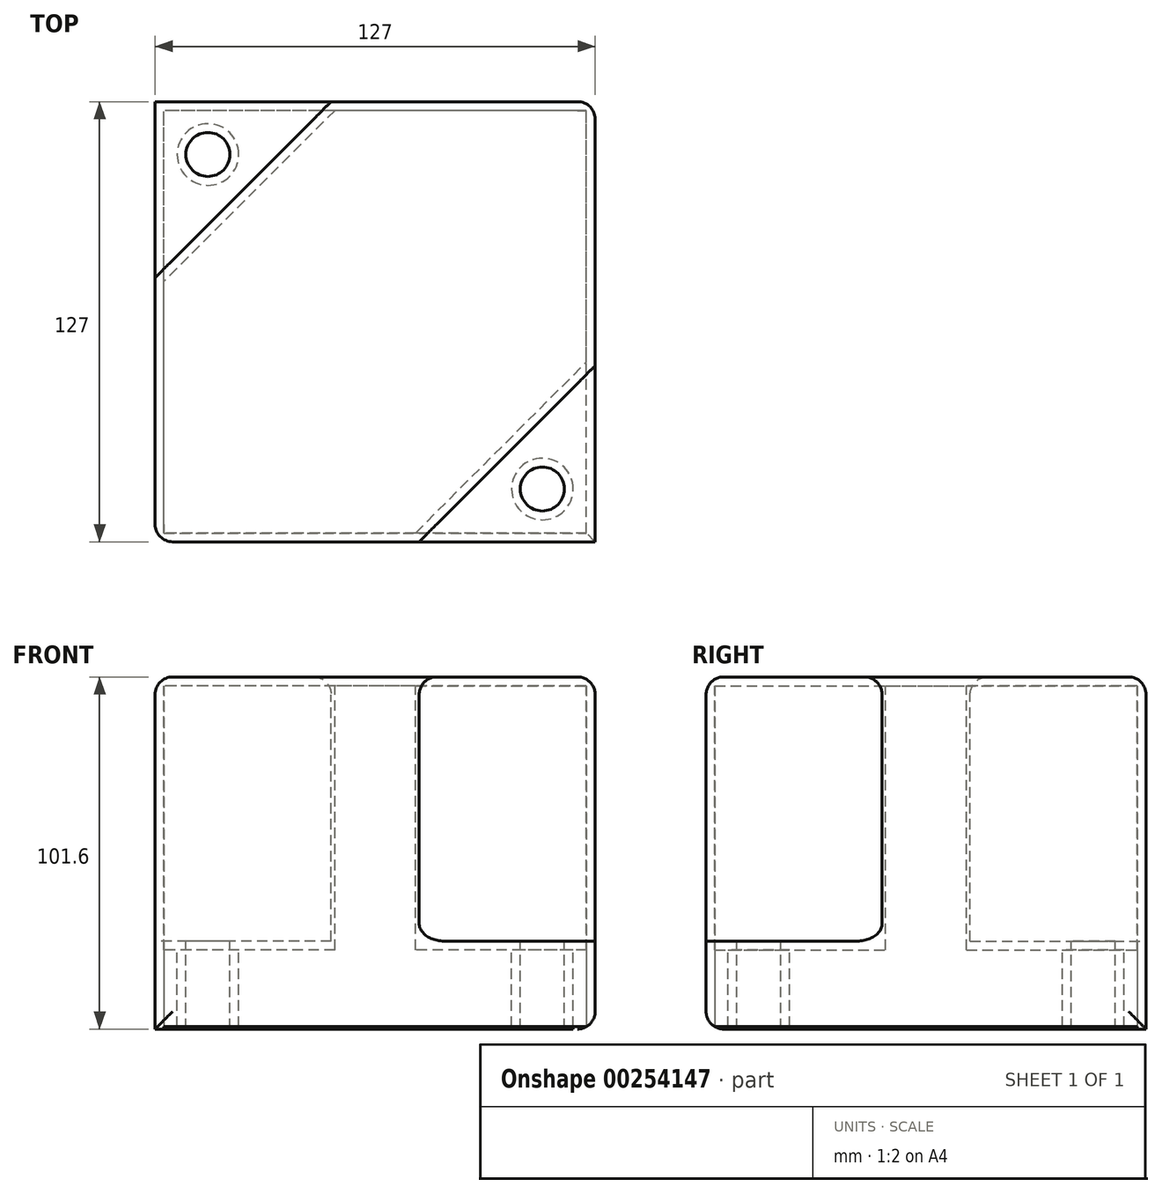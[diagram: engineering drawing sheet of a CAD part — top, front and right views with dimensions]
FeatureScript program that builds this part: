
annotation { "Feature Type Name" : "Feature", "Feature Type Description" : "" }
export const myFeature = defineFeature(function(context is Context, id is Id, definition is map)
    precondition{}
    {
        {
            var Q0;
            Q0=qCreatedBy(makeId("Top.planeOp"),FACE);
            var sketch = newSketch(context, id + "F0", { "sketchPlane" : qUnion([Q0])});
            skLineSegment(sketch, "E0.bottom", {"start": v(63.5, -63.5) * mm, "end": v(-63.5, -63.5) * mm});
            skLineSegment(sketch, "E0.top", {"start": v(63.5, 63.5) * mm, "end": v(-63.5, 63.5) * mm});
            skLineSegment(sketch, "E0.left", {"start": v(63.5, -63.5) * mm, "end": v(63.5, 63.5) * mm});
            skLineSegment(sketch, "E0.right", {"start": v(-63.5, -63.5) * mm, "end": v(-63.5, 63.5) * mm});
            skPoint(sketch, "E0.middle", {"position": v(0, 0) * mm});
            skSolve(sketch);
        }
        {
            var Q0;
            Q0=makeQuery(id+"F0.imprint","IMPRINT",FACE,{"disambiguationData":[TD([[makeQuery(id+"F0.imprint","IMPRINT",EDGE,{"derivedFrom":sQuery(id+"F0.wireOp",EDGE,"E0.bottom")}),-1.0]])]});
            extrude(context, id + "F1", {"entities" : qUnion([Q0]), "depth" : 101.6 * mm});
        }
        {
            var Q0;
            Q0=makeQuery(id+"F1.opExtrude","CAP_FACE",FACE,{"disambiguationData":[OSD([sQuery(id+"F0.wireOp",EDGE,"E0.bottom"),sQuery(id+"F0.wireOp",EDGE,"E0.top"),sQuery(id+"F0.wireOp",EDGE,"E0.left"),sQuery(id+"F0.wireOp",EDGE,"E0.right")])],"isStart":false});
            var sketch = newSketch(context, id + "F2", { "sketchPlane" : qUnion([Q0])});
            skLineSegment(sketch, "E1", {"start": v(-12.7, 63.5) * mm, "end": v(-63.5, 12.7) * mm});
            skLineSegment(sketch, "E2", {"start": v(12.7, -63.5) * mm, "end": v(63.5, -12.7) * mm});
            skSolve(sketch);
        }
        {
            var Q0;
            {var subQ0=sQuery(id+"F2.wireOp",EDGE,"E2");Q0=makeQuery(id+"F2.imprint","IMPRINT",FACE,{"disambiguationData":[TD([[makeQuery(id+"F2.imprint","IMPRINT",EDGE,{"derivedFrom":subQ0}),-1.0]])]});}
            var Q1;
            {var subQ0=sQuery(id+"F2.wireOp",EDGE,"E1");Q1=makeQuery(id+"F2.imprint","IMPRINT",FACE,{"disambiguationData":[TD([[makeQuery(id+"F2.imprint","IMPRINT",EDGE,{"derivedFrom":subQ0}),-1.0]])]});}
            extrude(context, id + "F3", {"entities" : qUnion([Q0, Q1]), "operationType" : NewBodyOperationType.REMOVE, "oppositeDirection" : true, "depth" : 76.2 * mm});
        }
        {
            var Q0;
            Q0=makeQuery(id+"F3.boolean.opBoolean","COPY",FACE,{"derivedFrom":makeQuery(id+"F3.opExtrude","CAP_FACE",FACE,{"disambiguationData":[OSD([sQuery(id+"F0.wireOp",EDGE,"E0.top"),sQuery(id+"F0.wireOp",EDGE,"E0.right"),sQuery(id+"F2.wireOp",EDGE,"E1")])],"isStart":false})});
            var sketch = newSketch(context, id + "F4", { "sketchPlane" : qUnion([Q0])});
            skCircle(sketch, "E3", {"center": v(-48.26, 48.26) * mm, "radius": 6.35 * mm});
            skCircle(sketch, "E4", {"center": v(48.26, -48.26) * mm, "radius": 6.35 * mm});
            skSolve(sketch);
        }
        {
            var Q0;
            Q0=makeQuery(id+"F4.imprint","IMPRINT",FACE,{"disambiguationData":[TD([[makeQuery(id+"F4.imprint","IMPRINT",EDGE,{"derivedFrom":sQuery(id+"F4.wireOp",EDGE,"E3")}),1.0]])]});
            var Q1;
            Q1=makeQuery(id+"F4.imprint","IMPRINT",FACE,{"disambiguationData":[TD([[makeQuery(id+"F4.imprint","IMPRINT",EDGE,{"derivedFrom":sQuery(id+"F4.wireOp",EDGE,"E4")}),1.0]])]});
            extrude(context, id + "F5", {"entities" : qUnion([Q0, Q1]), "operationType" : NewBodyOperationType.REMOVE, "oppositeDirection" : true, "depth" : 203.2 * mm});
        }
        {
            var Q0;
            Q0=makeQuery(id+"F1.opExtrude","CAP_FACE",FACE,{"disambiguationData":[OSD([sQuery(id+"F0.wireOp",EDGE,"E0.bottom"),sQuery(id+"F0.wireOp",EDGE,"E0.top"),sQuery(id+"F0.wireOp",EDGE,"E0.left"),sQuery(id+"F0.wireOp",EDGE,"E0.right")])],"isStart":true});
            shell(context, id + "F6", {"entities" : qUnion([Q0]), "thickness" : 2.54 * mm});
        }
        {
            var Q0;
            Q0=makeQuery(id+"F1.opExtrude","CAP_EDGE",EDGE,{"disambiguationData":[OSD([sQuery(id+"F0.wireOp",EDGE,"E0.right")])],"isStart":false});
            var Q1;
            Q1=makeQuery(id+"F1.opExtrude","CAP_EDGE",EDGE,{"disambiguationData":[OSD([sQuery(id+"F0.wireOp",EDGE,"E0.bottom")])],"isStart":false});
            var Q2;
            Q2=makeQuery(id+"F3.boolean.opBoolean","COPY",EDGE,{"derivedFrom":makeQuery(id+"F3.opExtrude","CAP_EDGE",EDGE,{"disambiguationData":[OSD([sQuery(id+"F2.wireOp",EDGE,"E2")])],"isStart":true})});
            var Q3;
            Q3=makeQuery(id+"F1.opExtrude","CAP_EDGE",EDGE,{"disambiguationData":[OSD([sQuery(id+"F0.wireOp",EDGE,"E0.left")])],"isStart":false});
            var Q4;
            Q4=makeQuery(id+"F1.opExtrude","CAP_EDGE",EDGE,{"disambiguationData":[OSD([sQuery(id+"F0.wireOp",EDGE,"E0.top")])],"isStart":false});
            var Q5;
            Q5=makeQuery(id+"F3.boolean.opBoolean","COPY",EDGE,{"derivedFrom":makeQuery(id+"F3.opExtrude","CAP_EDGE",EDGE,{"disambiguationData":[OSD([sQuery(id+"F2.wireOp",EDGE,"E1")])],"isStart":true})});
            var Q6;
            Q6=makeQuery(id+"F1.opExtrude","SWEPT_EDGE",EDGE,{"disambiguationData":[OSD([sQuery(id+"F0.wireOp",EDGE,"E0.bottom"),sQuery(id+"F0.wireOp",EDGE,"E0.right")])]});
            var Q7;
            Q7=makeQuery(id+"F3.boolean.opBoolean","COPY",EDGE,{"derivedFrom":makeQuery(id+"F3.opExtrude","SWEPT_EDGE",EDGE,{"disambiguationData":[OSD([sQuery(id+"F0.wireOp",EDGE,"E0.bottom"),sQuery(id+"F2.wireOp",EDGE,"E2")])]})});
            var Q8;
            Q8=makeQuery(id+"F3.boolean.opBoolean","COPY",EDGE,{"derivedFrom":makeQuery(id+"F3.opExtrude","SWEPT_EDGE",EDGE,{"disambiguationData":[OSD([sQuery(id+"F0.wireOp",EDGE,"E0.left"),sQuery(id+"F2.wireOp",EDGE,"E2")])]})});
            var Q9;
            Q9=makeQuery(id+"F1.opExtrude","SWEPT_EDGE",EDGE,{"disambiguationData":[OSD([sQuery(id+"F0.wireOp",EDGE,"E0.top"),sQuery(id+"F0.wireOp",EDGE,"E0.left")])]});
            var Q10;
            Q10=makeQuery(id+"F3.boolean.opBoolean","COPY",EDGE,{"derivedFrom":makeQuery(id+"F3.opExtrude","CAP_EDGE",EDGE,{"disambiguationData":[OSD([sQuery(id+"F0.wireOp",EDGE,"E0.bottom")])],"isStart":false})});
            var Q11;
            Q11=makeQuery(id+"F3.boolean.opBoolean","COPY",EDGE,{"derivedFrom":makeQuery(id+"F3.opExtrude","CAP_EDGE",EDGE,{"disambiguationData":[OSD([sQuery(id+"F0.wireOp",EDGE,"E0.left")])],"isStart":false})});
            var Q12;
            Q12=makeQuery(id+"F3.boolean.opBoolean","COPY",EDGE,{"derivedFrom":makeQuery(id+"F3.opExtrude","CAP_EDGE",EDGE,{"disambiguationData":[OSD([sQuery(id+"F2.wireOp",EDGE,"E2")])],"isStart":false})});
            var Q13;
            Q13=makeQuery(id+"F1.opExtrude","CAP_EDGE",EDGE,{"disambiguationData":[OSD([sQuery(id+"F0.wireOp",EDGE,"E0.left")])],"isStart":true});
            var Q14;
            Q14=makeQuery(id+"F1.opExtrude","CAP_EDGE",EDGE,{"disambiguationData":[OSD([sQuery(id+"F0.wireOp",EDGE,"E0.bottom")])],"isStart":true});
            fillet(context, id + "F7", {"entities" : qUnion([Q0, Q1, Q2, Q3, Q4, Q5, Q6, Q7, Q8, Q9, Q10, Q11, Q12, Q13, Q14]), "radius" : 5.08 * mm, "tangentPropagation" : true, "allowEdgeOverflow" : false});
        }
    });
